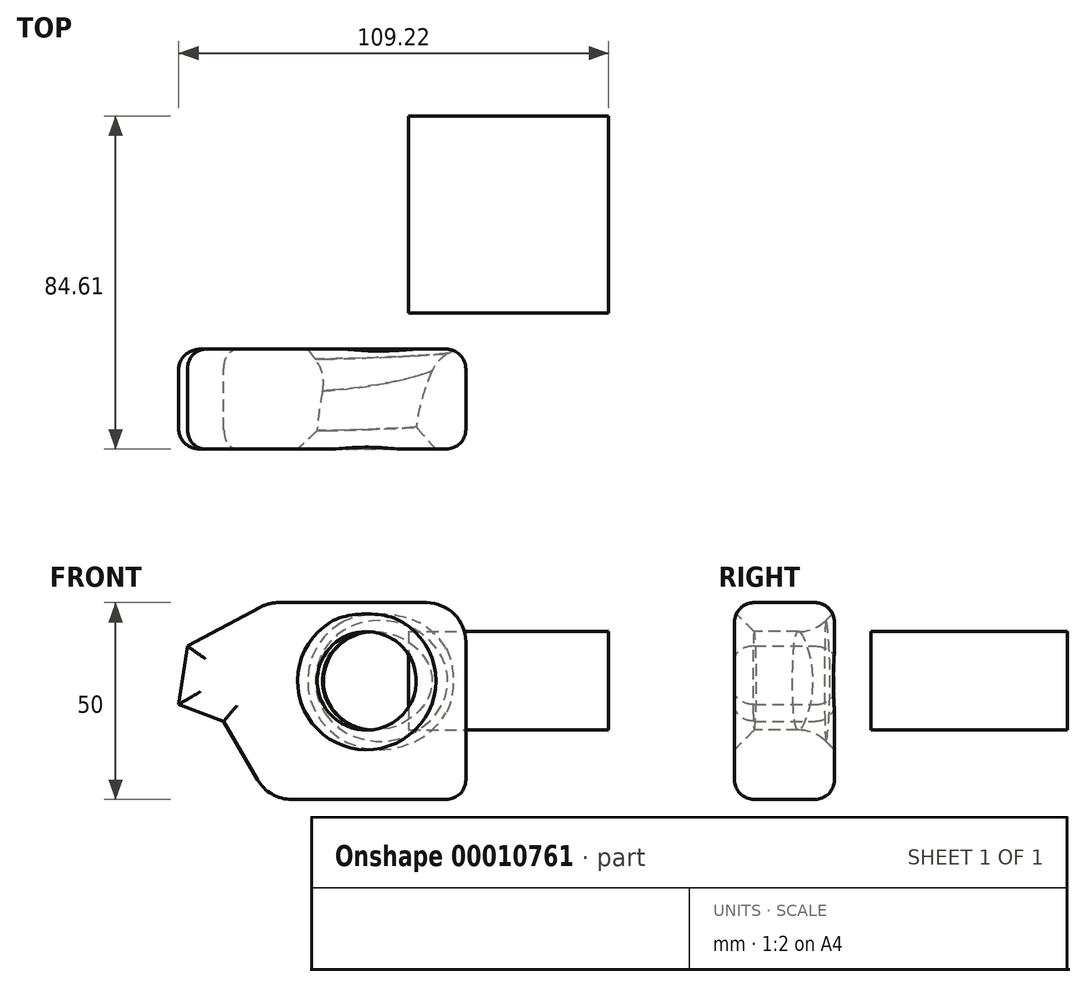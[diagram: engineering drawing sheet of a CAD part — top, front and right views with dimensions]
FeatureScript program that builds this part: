
annotation { "Feature Type Name" : "Feature", "Feature Type Description" : "" }
export const myFeature = defineFeature(function(context is Context, id is Id, definition is map)
    precondition{}
    {
        {
            var Q0;
            Q0=qCreatedBy(makeId("Front.planeOp"),FACE);
            var sketch = newSketch(context, id + "F0", { "sketchPlane" : qUnion([Q0])});
            skLineSegment(sketch, "E0.bottom", {"start": v(-24.6, 19.88) * mm, "end": v(25.4, 19.88) * mm});
            skLineSegment(sketch, "E0.top", {"start": v(-24.6, -30.12) * mm, "end": v(25.4, -30.12) * mm});
            skLineSegment(sketch, "E0.right", {"start": v(25.4, 19.88) * mm, "end": v(25.4, -30.12) * mm});
            skLineSegment(sketch, "E1", {"start": v(-24.6, 19.88) * mm, "end": v(-45.3, 8.83) * mm});
            skLineSegment(sketch, "E2", {"start": v(-45.3, 8.83) * mm, "end": v(-47.54, -6.01) * mm});
            skLineSegment(sketch, "E3", {"start": v(-47.54, -6.01) * mm, "end": v(-36.07, -10.25) * mm});
            skLineSegment(sketch, "E4", {"start": v(-36.07, -10.25) * mm, "end": v(-24.6, -30.12) * mm});
            skSolve(sketch);
        }
        {
            var Q0;
            Q0=makeQuery(id+"F0.imprint","IMPRINT",FACE,{"disambiguationData":[TD([[makeQuery(id+"F0.imprint","IMPRINT",EDGE,{"derivedFrom":sQuery(id+"F0.wireOp",EDGE,"E0.bottom")}),-1.0]])]});
            extrude(context, id + "F1", {"entities" : qUnion([Q0]), "endBound" : BoundingType.SYMMETRIC, "depth" : 25.4 * mm});
        }
        {
            var Q0;
            Q0=makeQuery(id+"F1.opExtrude","SWEPT_EDGE",EDGE,{"disambiguationData":[OSD([sQuery(id+"F0.wireOp",EDGE,"E0.bottom"),sQuery(id+"F0.wireOp",EDGE,"E1")])]});
            var Q1;
            Q1=makeQuery(id+"F1.opExtrude","SWEPT_EDGE",EDGE,{"disambiguationData":[OSD([sQuery(id+"F0.wireOp",EDGE,"E0.bottom"),sQuery(id+"F0.wireOp",EDGE,"E0.right")])]});
            var Q2;
            Q2=makeQuery(id+"F1.opExtrude","SWEPT_EDGE",EDGE,{"disambiguationData":[OSD([sQuery(id+"F0.wireOp",EDGE,"E0.top"),sQuery(id+"F0.wireOp",EDGE,"E4")])]});
            fillet(context, id + "F2", {"entities" : qUnion([Q0, Q1, Q2]), "radius" : 10 * mm, "tangentPropagation" : true, "allowEdgeOverflow" : false});
        }
        {
            var Q0;
            Q0=makeQuery(id+"F1.opExtrude","CAP_FACE",FACE,{"disambiguationData":[OSD([sQuery(id+"F0.wireOp",EDGE,"E0.bottom"),sQuery(id+"F0.wireOp",EDGE,"E0.top"),sQuery(id+"F0.wireOp",EDGE,"E0.right"),sQuery(id+"F0.wireOp",EDGE,"E1"),sQuery(id+"F0.wireOp",EDGE,"E2"),sQuery(id+"F0.wireOp",EDGE,"E3"),sQuery(id+"F0.wireOp",EDGE,"E4")])],"isStart":false});
            var sketch = newSketch(context, id + "F3", { "sketchPlane" : qUnion([Q0])});
            skCircle(sketch, "E5", {"center": v(0, 0) * mm, "radius": 12.5 * mm});
            skLineSegment(sketch, "E6", {"start": v(60, 35.25) * mm, "end": v(60, -32.57) * mm, "construction": true});
            skSolve(sketch);
        }
        {
            var Q0;
            Q0=makeQuery(id+"F3.imprint","IMPRINT",FACE,{"disambiguationData":[TD([[makeQuery(id+"F3.imprint","IMPRINT",EDGE,{"derivedFrom":sQuery(id+"F3.wireOp",EDGE,"E5")}),-1.0]])]});
            var sketch = newSketch(context, id + "F4", { "sketchPlane" : qUnion([Q0])});
            skLineSegment(sketch, "E7.0", {"start": v(60, 35.25) * mm, "end": v(60, -32.57) * mm});
            skSolve(sketch);
        }
        {
            var Q0;
            Q0=makeQuery(id+"F3.imprint","IMPRINT",FACE,{"disambiguationData":[TD([[makeQuery(id+"F3.imprint","IMPRINT",EDGE,{"derivedFrom":sQuery(id+"F3.wireOp",EDGE,"E5")}),1.0]])]});
            var Q1;
            Q1=sQuery(id+"F4.wireOp",EDGE,"E7.0");
            revolve(context, id + "F5", {"operationType" : NewBodyOperationType.REMOVE, "entities" : qUnion([Q0]), "axis" : qUnion([Q1]), "revolveType" : RevolveType.FULL, "oppositeDirection" : true});
        }
        {
            var Q0;
            Q0=makeQuery(id+"F5.boolean.opBoolean","INTERSECT",EDGE,{"derivedFrom":[makeQuery(id+"F1.opExtrude","CAP_FACE",FACE,{"disambiguationData":[OSD([sQuery(id+"F0.wireOp",EDGE,"E0.bottom"),sQuery(id+"F0.wireOp",EDGE,"E0.top"),sQuery(id+"F0.wireOp",EDGE,"E0.right"),sQuery(id+"F0.wireOp",EDGE,"E1"),sQuery(id+"F0.wireOp",EDGE,"E2"),sQuery(id+"F0.wireOp",EDGE,"E3"),sQuery(id+"F0.wireOp",EDGE,"E4")])],"isStart":false}),makeQuery(id+"F5.opRevolve","SWEPT_FACE",FACE,{"disambiguationData":[OSD([sQuery(id+"F3.wireOp",EDGE,"E5")])]})]});
            var Q1;
            Q1=makeQuery(id+"F5.boolean.opBoolean","INTERSECT",EDGE,{"derivedFrom":[makeQuery(id+"F1.opExtrude","CAP_FACE",FACE,{"disambiguationData":[OSD([sQuery(id+"F0.wireOp",EDGE,"E0.bottom"),sQuery(id+"F0.wireOp",EDGE,"E0.top"),sQuery(id+"F0.wireOp",EDGE,"E0.right"),sQuery(id+"F0.wireOp",EDGE,"E1"),sQuery(id+"F0.wireOp",EDGE,"E2"),sQuery(id+"F0.wireOp",EDGE,"E3"),sQuery(id+"F0.wireOp",EDGE,"E4")])],"isStart":true}),makeQuery(id+"F5.opRevolve","SWEPT_FACE",FACE,{"disambiguationData":[OSD([sQuery(id+"F3.wireOp",EDGE,"E5")])]})]});
            chamfer(context, id + "F6", {"entities" : qUnion([Q0, Q1]), "width" : 5 * mm, "tangentPropagation" : true});
        }
        {
            var Q0;
            {var subQ0=sQuery(id+"F0.wireOp",EDGE,"E0.bottom");var subQ1=sQuery(id+"F0.wireOp",EDGE,"E1");Q0=makeQuery(id+"F2.opFillet","BLEND_EDGE",EDGE,{"blendedFrom":[makeQuery(id+"F1.opExtrude","SWEPT_EDGE",EDGE,{"disambiguationData":[OSD([subQ0,subQ1])]}),makeQuery(id+"F1.opExtrude","CAP_FACE",FACE,{"disambiguationData":[OSD([subQ0,sQuery(id+"F0.wireOp",EDGE,"E0.top"),sQuery(id+"F0.wireOp",EDGE,"E0.right"),subQ1,sQuery(id+"F0.wireOp",EDGE,"E2"),sQuery(id+"F0.wireOp",EDGE,"E3"),sQuery(id+"F0.wireOp",EDGE,"E4")])],"isStart":false})],"blendedInto":[makeQuery(id+"F1.opExtrude","CAP_FACE",FACE,{"disambiguationData":[OSD([subQ0,sQuery(id+"F0.wireOp",EDGE,"E0.top"),sQuery(id+"F0.wireOp",EDGE,"E0.right"),subQ1,sQuery(id+"F0.wireOp",EDGE,"E2"),sQuery(id+"F0.wireOp",EDGE,"E3"),sQuery(id+"F0.wireOp",EDGE,"E4")])],"isStart":false})]});}
            var Q1;
            Q1=makeQuery(id+"F1.opExtrude","CAP_EDGE",EDGE,{"disambiguationData":[OSD([sQuery(id+"F0.wireOp",EDGE,"E2")])],"isStart":false});
            var Q2;
            Q2=makeQuery(id+"F1.opExtrude","CAP_EDGE",EDGE,{"disambiguationData":[OSD([sQuery(id+"F0.wireOp",EDGE,"E3")])],"isStart":false});
            var Q3;
            Q3=makeQuery(id+"F1.opExtrude","CAP_EDGE",EDGE,{"disambiguationData":[OSD([sQuery(id+"F0.wireOp",EDGE,"E4")])],"isStart":false});
            var Q4;
            {var subQ0=sQuery(id+"F0.wireOp",EDGE,"E0.top");var subQ1=sQuery(id+"F0.wireOp",EDGE,"E4");Q4=makeQuery(id+"F2.opFillet","BLEND_EDGE",EDGE,{"blendedFrom":[makeQuery(id+"F1.opExtrude","SWEPT_EDGE",EDGE,{"disambiguationData":[OSD([subQ0,subQ1])]}),makeQuery(id+"F1.opExtrude","CAP_FACE",FACE,{"disambiguationData":[OSD([sQuery(id+"F0.wireOp",EDGE,"E0.bottom"),subQ0,sQuery(id+"F0.wireOp",EDGE,"E0.right"),sQuery(id+"F0.wireOp",EDGE,"E1"),sQuery(id+"F0.wireOp",EDGE,"E2"),sQuery(id+"F0.wireOp",EDGE,"E3"),subQ1])],"isStart":true})],"blendedInto":[makeQuery(id+"F1.opExtrude","CAP_FACE",FACE,{"disambiguationData":[OSD([sQuery(id+"F0.wireOp",EDGE,"E0.bottom"),subQ0,sQuery(id+"F0.wireOp",EDGE,"E0.right"),sQuery(id+"F0.wireOp",EDGE,"E1"),sQuery(id+"F0.wireOp",EDGE,"E2"),sQuery(id+"F0.wireOp",EDGE,"E3"),subQ1])],"isStart":true})]});}
            var Q5;
            Q5=makeQuery(id+"F1.opExtrude","CAP_EDGE",EDGE,{"disambiguationData":[OSD([sQuery(id+"F0.wireOp",EDGE,"E3")])],"isStart":true});
            var Q6;
            Q6=makeQuery(id+"F1.opExtrude","CAP_EDGE",EDGE,{"disambiguationData":[OSD([sQuery(id+"F0.wireOp",EDGE,"E2")])],"isStart":true});
            var Q7;
            Q7=makeQuery(id+"F1.opExtrude","CAP_EDGE",EDGE,{"disambiguationData":[OSD([sQuery(id+"F0.wireOp",EDGE,"E1")])],"isStart":true});
            fillet(context, id + "F7", {"entities" : qUnion([Q0, Q1, Q2, Q3, Q4, Q5, Q6, Q7]), "radius" : 5 * mm, "tangentPropagation" : true, "allowEdgeOverflow" : false});
        }
        {
            var Q0;
            Q0=qCreatedBy(makeId("Top.planeOp"),FACE);
            var sketch = newSketch(context, id + "F8", { "sketchPlane" : qUnion([Q0])});
            skCircle(sketch, "E8", {"center": v(71.09, 0) * mm, "radius": 18.27 * mm});
            skSolve(sketch);
        }
        {
            var Q0;
            Q0=makeQuery(id+"F8.imprint","IMPRINT",FACE,{"disambiguationData":[TD([[makeQuery(id+"F8.imprint","IMPRINT",EDGE,{"derivedFrom":sQuery(id+"F8.wireOp",EDGE,"E8")}),1.0]])]});
            extrude(context, id + "F9", {"entities" : qUnion([Q0]), "depth" : 25 * mm});
        }
        {
            var Q0;
            Q0=makeQuery(id+"F9.opExtrude","SWEPT_BODY",BODY,{"disambiguationData":[OSD([sQuery(id+"F8.wireOp",EDGE,"E8")])]});
            deleteBodies(context, id + "F10", {"entities" : qUnion([Q0])});
        }
        {
            var Q0;
            Q0=makeQuery(id+"F7.opFillet","BLEND_EDGE",EDGE,{"blendedFrom":[makeQuery(id+"F1.opExtrude","CAP_EDGE",EDGE,{"disambiguationData":[OSD([sQuery(id+"F0.wireOp",EDGE,"E0.top")])],"isStart":false}),makeQuery(id+"F1.opExtrude","CAP_EDGE",EDGE,{"disambiguationData":[OSD([sQuery(id+"F0.wireOp",EDGE,"E0.right")])],"isStart":false})],"blendedInto":[]});
            fillet(context, id + "F11", {"entities" : qUnion([Q0]), "radius" : 5 * mm, "tangentPropagation" : true, "allowEdgeOverflow" : false});
        }
        {
            var Q0;
            {var subQ0=makeQuery(id+"F5.opRevolve","SWEPT_FACE",FACE,{"disambiguationData":[OSD([sQuery(id+"F3.wireOp",EDGE,"E5")])]});Q0=makeQuery(id+"F6.opChamfer","BLEND_EDGE",EDGE,{"blendedFrom":[makeQuery(id+"F5.boolean.opBoolean","INTERSECT",EDGE,{"derivedFrom":[makeQuery(id+"F1.opExtrude","CAP_FACE",FACE,{"disambiguationData":[OSD([sQuery(id+"F0.wireOp",EDGE,"E0.bottom"),sQuery(id+"F0.wireOp",EDGE,"E0.top"),sQuery(id+"F0.wireOp",EDGE,"E0.right"),sQuery(id+"F0.wireOp",EDGE,"E1"),sQuery(id+"F0.wireOp",EDGE,"E2"),sQuery(id+"F0.wireOp",EDGE,"E3"),sQuery(id+"F0.wireOp",EDGE,"E4")])],"isStart":true}),subQ0]}),makeQuery(id+"F5.boolean.opBoolean","COPY",FACE,{"derivedFrom":subQ0})],"blendedInto":[makeQuery(id+"F5.boolean.opBoolean","COPY",FACE,{"derivedFrom":subQ0})]});}
            fillet(context, id + "F12", {"entities" : qUnion([Q0]), "radius" : 10 * mm, "tangentPropagation" : true, "allowEdgeOverflow" : false});
        }
        {
            var Q0;
            Q0=qCreatedBy(makeId("Top.planeOp"),FACE);
            var sketch = newSketch(context, id + "F13", { "sketchPlane" : qUnion([Q0])});
            skLineSegment(sketch, "E9.bottom", {"start": v(10.88, 71.9) * mm, "end": v(61.68, 71.9) * mm});
            skLineSegment(sketch, "E9.top", {"start": v(10.88, 21.9) * mm, "end": v(61.68, 21.9) * mm});
            skLineSegment(sketch, "E9.left", {"start": v(10.88, 71.9) * mm, "end": v(10.88, 21.9) * mm});
            skLineSegment(sketch, "E9.right", {"start": v(61.68, 71.9) * mm, "end": v(61.68, 21.9) * mm});
            skSolve(sketch);
        }
        {
            var Q0;
            Q0=makeQuery(id+"F13.imprint","IMPRINT",FACE,{"disambiguationData":[TD([[makeQuery(id+"F13.imprint","IMPRINT",EDGE,{"derivedFrom":sQuery(id+"F13.wireOp",EDGE,"E9.bottom")}),-1.0]])]});
            extrude(context, id + "F14", {"entities" : qUnion([Q0]), "endBound" : BoundingType.SYMMETRIC, "depth" : 25 * mm});
        }
    });
